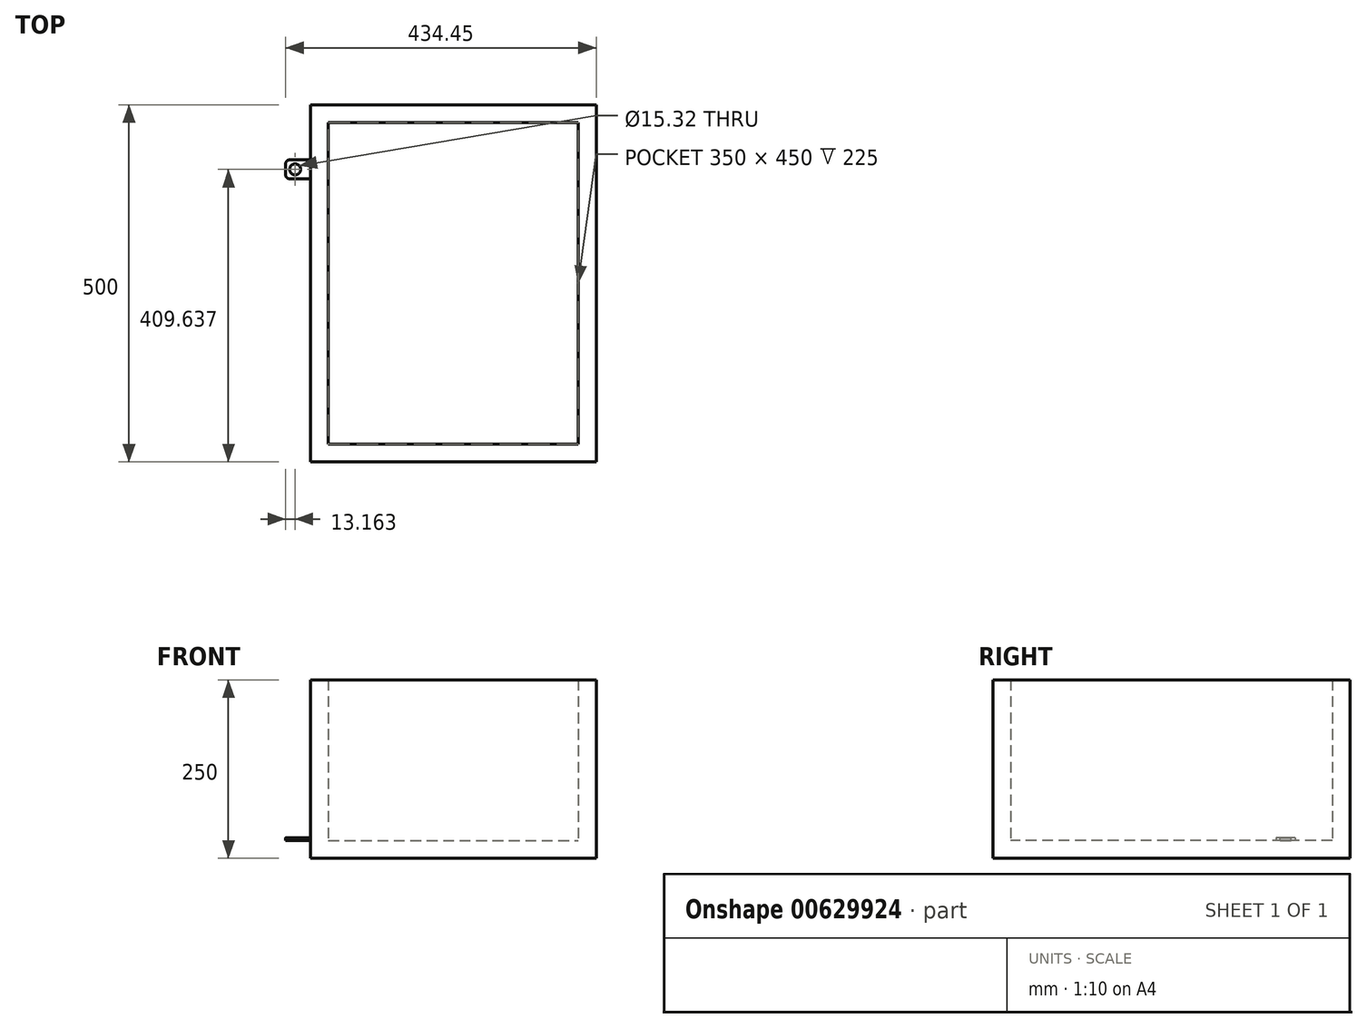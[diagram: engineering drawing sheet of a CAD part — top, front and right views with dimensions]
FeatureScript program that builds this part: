
annotation { "Feature Type Name" : "Feature", "Feature Type Description" : "" }
export const myFeature = defineFeature(function(context is Context, id is Id, definition is map)
    precondition{}
    {
        {
            var Q0;
            Q0=qCreatedBy(makeId("Top.planeOp"),FACE);
            var sketch = newSketch(context, id + "F0", { "sketchPlane" : qUnion([Q0])});
            skLineSegment(sketch, "E0.bottom", {"start": v(-198.32, 265.24) * mm, "end": v(201.68, 265.24) * mm});
            skLineSegment(sketch, "E0.top", {"start": v(-198.32, -234.76) * mm, "end": v(201.68, -234.76) * mm});
            skLineSegment(sketch, "E0.left", {"start": v(-198.32, 265.24) * mm, "end": v(-198.32, -234.76) * mm});
            skLineSegment(sketch, "E0.right", {"start": v(201.68, 265.24) * mm, "end": v(201.68, -234.76) * mm});
            skSolve(sketch);
        }
        {
            var Q0;
            Q0=makeQuery(id+"F0.imprint","IMPRINT",FACE,{"disambiguationData":[TD([[makeQuery(id+"F0.imprint","IMPRINT",EDGE,{"derivedFrom":sQuery(id+"F0.wireOp",EDGE,"E0.bottom")}),-1.0]])]});
            extrude(context, id + "F1", {"entities" : qUnion([Q0]), "depth" : 250 * mm, "offsetDistance" : 25 * mm});
        }
        {
            var Q0;
            Q0=makeQuery(id+"F1.opExtrude","CAP_FACE",FACE,{"disambiguationData":[OSD([sQuery(id+"F0.wireOp",EDGE,"E0.bottom"),sQuery(id+"F0.wireOp",EDGE,"E0.top"),sQuery(id+"F0.wireOp",EDGE,"E0.left"),sQuery(id+"F0.wireOp",EDGE,"E0.right")])],"isStart":false});
            shell(context, id + "F2", {"entities" : qUnion([Q0]), "thickness" : 25 * mm});
        }
        {
            var Q0;
            Q0=makeQuery(id+"F2.opShell","OFFSET_FACE",FACE,{"disambiguationData":[OSD([sQuery(id+"F0.wireOp",EDGE,"E0.bottom"),sQuery(id+"F0.wireOp",EDGE,"E0.top"),sQuery(id+"F0.wireOp",EDGE,"E0.left"),sQuery(id+"F0.wireOp",EDGE,"E0.right")])]});
            var sketch = newSketch(context, id + "F3", { "sketchPlane" : qUnion([Q0])});
            skLineSegment(sketch, "E1.bottom", {"start": v(-173.32, 188.01) * mm, "end": v(-232.77, 188.01) * mm});
            skLineSegment(sketch, "E1.top", {"start": v(-173.32, 161.74) * mm, "end": v(-232.77, 161.74) * mm});
            skLineSegment(sketch, "E1.left", {"start": v(-173.32, 188.01) * mm, "end": v(-173.32, 161.74) * mm});
            skLineSegment(sketch, "E1.right", {"start": v(-232.77, 188.01) * mm, "end": v(-232.77, 161.74) * mm});
            skSolve(sketch);
        }
        {
            var Q0;
            Q0=makeQuery(id+"F3.imprint","IMPRINT",FACE,{"disambiguationData":[TD([[makeQuery(id+"F3.imprint","IMPRINT",EDGE,{"derivedFrom":sQuery(id+"F3.wireOp",EDGE,"E1.bottom")}),1.0]])]});
            extrude(context, id + "F4", {"entities" : qUnion([Q0]), "operationType" : NewBodyOperationType.ADD, "depth" : 4 * mm, "offsetDistance" : 25 * mm});
        }
        {
            var Q0;
            Q0=makeQuery(id+"F4.opExtrude","SWEPT_EDGE",EDGE,{"disambiguationData":[OSD([sQuery(id+"F3.wireOp",EDGE,"E1.top"),sQuery(id+"F3.wireOp",EDGE,"E1.right")])]});
            var Q1;
            Q1=makeQuery(id+"F4.opExtrude","SWEPT_EDGE",EDGE,{"disambiguationData":[OSD([sQuery(id+"F3.wireOp",EDGE,"E1.bottom"),sQuery(id+"F3.wireOp",EDGE,"E1.right")])]});
            fillet(context, id + "F5", {"entities" : qUnion([Q0, Q1]), "radius" : 5 * mm, "tangentPropagation" : true, "allowEdgeOverflow" : false});
        }
        {
            var Q0;
            Q0=makeQuery(id+"F4.opExtrude","CAP_FACE",FACE,{"disambiguationData":[OSD([sQuery(id+"F3.wireOp",EDGE,"E1.bottom"),sQuery(id+"F3.wireOp",EDGE,"E1.top"),sQuery(id+"F3.wireOp",EDGE,"E1.left"),sQuery(id+"F3.wireOp",EDGE,"E1.right")])],"isStart":false});
            var sketch = newSketch(context, id + "F6", { "sketchPlane" : qUnion([Q0])});
            skCircle(sketch, "E2", {"center": v(-219.6, 174.88) * mm, "radius": 7.66 * mm});
            skPoint(sketch, "E2.centerSnap0", {"position": v(-232.77, 174.88) * mm});
            skSolve(sketch);
        }
        {
            var Q0;
            Q0=makeQuery(id+"F6.imprint","IMPRINT",FACE,{"disambiguationData":[TD([[makeQuery(id+"F6.imprint","IMPRINT",EDGE,{"derivedFrom":sQuery(id+"F6.wireOp",EDGE,"E2")}),1.0]])]});
            extrude(context, id + "F7", {"entities" : qUnion([Q0]), "operationType" : NewBodyOperationType.REMOVE, "oppositeDirection" : true, "depth" : 25 * mm, "offsetDistance" : 25 * mm});
        }
    });
